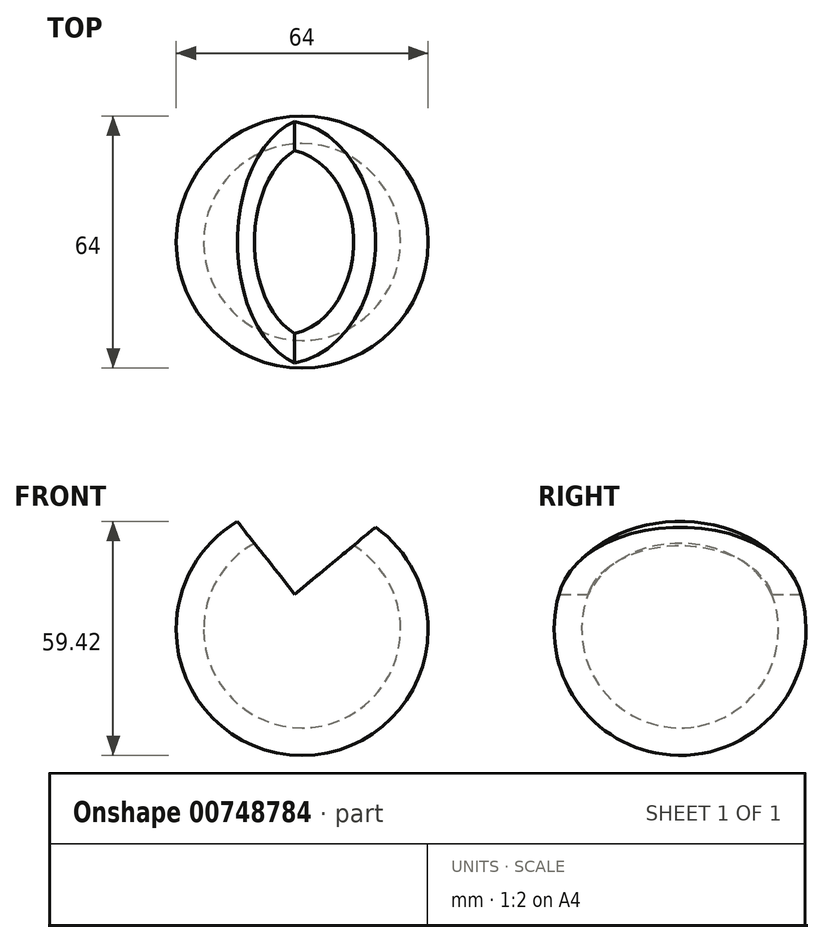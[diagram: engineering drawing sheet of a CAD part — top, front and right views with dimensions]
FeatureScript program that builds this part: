
annotation { "Feature Type Name" : "Feature", "Feature Type Description" : "" }
export const myFeature = defineFeature(function(context is Context, id is Id, definition is map)
    precondition{}
    {
        {
            var Q0;
            Q0=qCreatedBy(makeId("Top.planeOp"),FACE);
            var sketch = newSketch(context, id + "F0", { "sketchPlane" : qUnion([Q0])});
            skCircle(sketch, "E0", {"center": v(0, 0) * mm, "radius": 21.26 * mm});
            skCircle(sketch, "E1.1.0", {"center": v(20.92, -11.1) * mm, "radius": 4.2 * mm});
            skCircle(sketch, "E1.1.1", {"center": v(17.03, -16.45) * mm, "radius": 2.42 * mm});
            skCircle(sketch, "E1.2.0", {"center": v(-11.1, -20.92) * mm, "radius": 4.2 * mm});
            skCircle(sketch, "E1.2.1", {"center": v(-16.45, -17.03) * mm, "radius": 2.42 * mm});
            skCircle(sketch, "E1.3.0", {"center": v(-20.92, 11.1) * mm, "radius": 4.2 * mm});
            skCircle(sketch, "E1.3.1", {"center": v(-17.03, 16.45) * mm, "radius": 2.42 * mm});
            skLineSegment(sketch, "E1.anchor1", {"start": v(0, 0) * mm, "end": v(11.1, 20.92) * mm, "construction": true});
            skLineSegment(sketch, "E1.anchor2", {"start": v(0, 0) * mm, "end": v(-20.92, 11.1) * mm, "construction": true});
            skLineSegment(sketch, "E2", {"start": v(-17.56, 18.82) * mm, "end": v(10.2, 25.01) * mm});
            skLineSegment(sketch, "E3", {"start": v(-10.2, -25.01) * mm, "end": v(17.56, -18.82) * mm});
            skArc(sketch, "E4", {"start": v(14.5, 18.45) * mm, "mid": v(14.04, 16.82) * mm, "end": v(14.77, 15.29) * mm});
            skArc(sketch, "E5", {"start": v(14.77, 15.29) * mm, "mid": v(18.87, 17.24) * mm, "end": v(14.5, 18.45) * mm});
            skArc(sketch, "E6", {"start": v(10.2, 25.01) * mm, "mid": v(7.6, 18.62) * mm, "end": v(14.5, 18.45) * mm});
            skArc(sketch, "E7", {"start": v(14.5, 18.45) * mm, "mid": v(14.61, 23.22) * mm, "end": v(10.2, 25.01) * mm});
            skArc(sketch, "E8", {"start": v(174.54, -63.97) * mm, "mid": v(149.54, -38.97) * mm, "end": v(124.54, -63.97) * mm});
            skLineSegment(sketch, "E9", {"start": v(124.54, -63.97) * mm, "end": v(174.54, -63.97) * mm});
            skArc(sketch, "E10", {"start": v(181.54, -63.97) * mm, "mid": v(149.54, -31.97) * mm, "end": v(117.54, -63.97) * mm});
            skLineSegment(sketch, "E11", {"start": v(124.54, -63.97) * mm, "end": v(117.54, -63.97) * mm});
            skLineSegment(sketch, "E12", {"start": v(174.54, -63.97) * mm, "end": v(181.54, -63.97) * mm});
            skSolve(sketch);
        }
        {
            var Q0;
            Q0=makeQuery(id+"F0.imprint","IMPRINT",FACE,{"disambiguationData":[TD([[makeQuery(id+"F0.imprint","IMPRINT",EDGE,{"derivedFrom":sQuery(id+"F0.wireOp",EDGE,"E8")}),-1.0]])]});
            var Q1;
            Q1=sQuery(id+"F0.wireOp",EDGE,"E9");
            revolve(context, id + "F1", {"surfaceOperationType" : NewSurfaceOperationType.NEW, "entities" : qUnion([Q0]), "axis" : qUnion([Q1]), "revolveType" : RevolveType.FULL});
        }
        {
            var Q0;
            Q0=qCreatedBy(makeId("Front.planeOp"),FACE);
            var sketch = newSketch(context, id + "F2", { "sketchPlane" : qUnion([Q0])});
            skLineSegment(sketch, "E13", {"start": v(119.32, 44.8) * mm, "end": v(147.66, 8.92) * mm});
            skLineSegment(sketch, "E14", {"start": v(147.66, 8.92) * mm, "end": v(190.9, 44.8) * mm});
            skLineSegment(sketch, "E15", {"start": v(190.9, 44.8) * mm, "end": v(119.32, 44.8) * mm});
            skSolve(sketch);
        }
        {
            var Q0;
            Q0=makeQuery(id+"F2.imprint","IMPRINT",FACE,{"disambiguationData":[TD([[makeQuery(id+"F2.imprint","IMPRINT",EDGE,{"derivedFrom":sQuery(id+"F2.wireOp",EDGE,"E13")}),1.0]])]});
            extrude(context, id + "F3", {"entities" : qUnion([Q0]), "operationType" : NewBodyOperationType.REMOVE, "depth" : 115.6 * mm, "offsetDistance" : 25 * mm});
        }
    });
